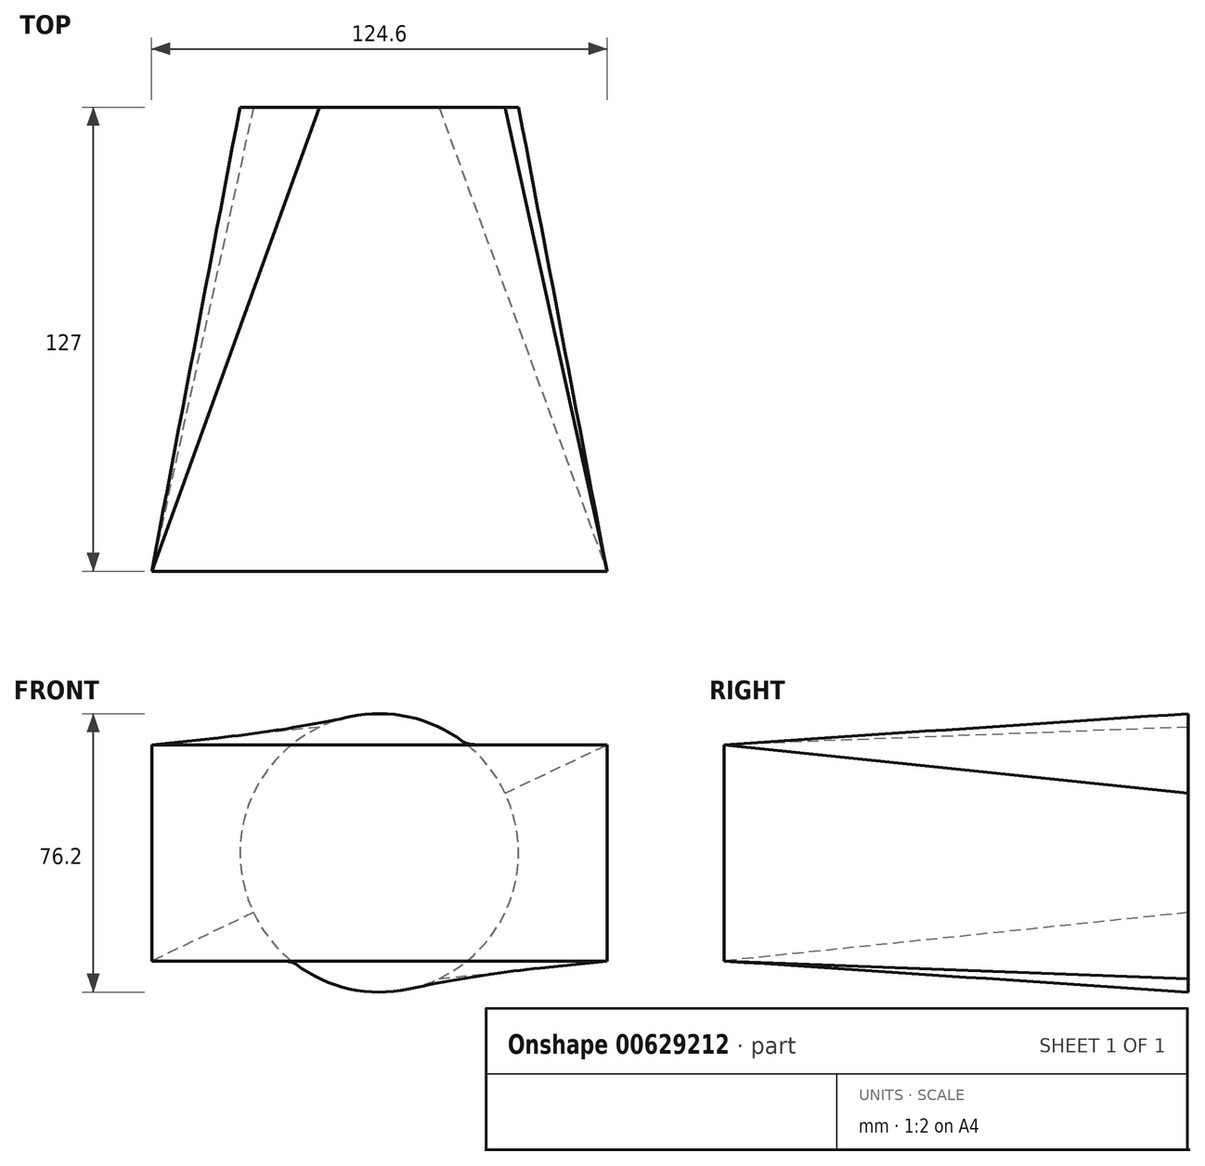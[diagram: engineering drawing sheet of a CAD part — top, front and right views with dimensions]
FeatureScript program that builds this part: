
annotation { "Feature Type Name" : "Feature", "Feature Type Description" : "" }
export const myFeature = defineFeature(function(context is Context, id is Id, definition is map)
    precondition{}
    {
        {
            var Q0;
            Q0=qCreatedBy(makeId("Front.planeOp"),FACE);
            var sketch = newSketch(context, id + "F0", { "sketchPlane" : qUnion([Q0])});
            skCircle(sketch, "E0", {"center": v(0, 0) * mm, "radius": 38.1 * mm});
            skSolve(sketch);
        }
        {
            var Q0;
            Q0=qCreatedBy(makeId("Front.planeOp"),FACE);
            cPlane(context, id + "F1", {"entities" : qUnion([Q0]), "cplaneType" : CPlaneType.OFFSET, "offset" : 127 * mm, "width" : 152.4 * mm, "height" : 152.4 * mm});
        }
        {
            var Q0;
            Q0=qCreatedBy(id+"F1.planeOp",FACE);
            var sketch = newSketch(context, id + "F2", { "sketchPlane" : qUnion([Q0])});
            skLineSegment(sketch, "E1.bottom", {"start": v(62.3, 29.59) * mm, "end": v(-62.3, 29.59) * mm});
            skLineSegment(sketch, "E1.top", {"start": v(62.3, -29.59) * mm, "end": v(-62.3, -29.59) * mm});
            skLineSegment(sketch, "E1.left", {"start": v(62.3, 29.59) * mm, "end": v(62.3, -29.59) * mm});
            skLineSegment(sketch, "E1.right", {"start": v(-62.3, 29.59) * mm, "end": v(-62.3, -29.59) * mm});
            skPoint(sketch, "E1.middle", {"position": v(0, 0) * mm});
            skSolve(sketch);
        }
        {
            var Q0;
            Q0=makeQuery(id+"F0.imprint","IMPRINT",FACE,{"disambiguationData":[TD([[makeQuery(id+"F0.imprint","IMPRINT",EDGE,{"derivedFrom":sQuery(id+"F0.wireOp",EDGE,"E0")}),1.0]])]});
            var Q1;
            Q1=makeQuery(id+"F2.imprint","IMPRINT",FACE,{"disambiguationData":[TD([[makeQuery(id+"F2.imprint","IMPRINT",EDGE,{"derivedFrom":sQuery(id+"F2.wireOp",EDGE,"E1.bottom")}),1.0]])]});
            loft(context, id + "F3", {"sheetProfilesArray" : [{ "sheetProfileEntities" : qUnion([Q0]) }, { "sheetProfileEntities" : qUnion([Q1]) }]});
        }
    });
